# Revit family: Shower-Wall_Supply_Elbow-KOHLER-STATEMENT_WAND-26289W
name_source: partatom
category: Plumbing Fixtures
revit_build: Autodesk Revit 2017 (Build: 20160225_1515(x64)
units: mm (PartAtom-declared; Revit-internal decimal feet)

## family parameters
Cut with Voids When Loaded = No
Host = Face
OmniClass Number = 23.31.17.00
OmniClass Title = Showers
Part Type = Normal
Room Calculation Point = No
Round Connector Dimension = Use Diameter
Shared = No

## types (5) — shared parameters
ADA Compliant = No
Assembly Code = D2010700
CW Connection = No
Cold Water Inlet = Cold Water Inlet
Date Modified = 11/22/2021
Default Elevation = 42"
Description = STATEMENT WAND HS HOLDER W/ SUPPLY
Drain Included = No
Flow Rate = 0 GPM
HW Connection = Yes
Handle Clearance = 2 3/8"
Height = 3 3/4"
Hot Water Inlet = Hot Water Inlet
Length = 2 3/8"
Manufacturer = KOHLER Co.
Master Format 2014 = 22 42 23
Master Format 2014 Name = Residential Showers
Material = Premium Metal Construction
Pressure = 0.00 psi
Product Name = STATEMENT_WAND
Tempered Water Inlet = Tempered Water Inlet
URL = https://www.kohler.co.uk
Vent Connection = No
Waste Connection = No
Waste Water Outlet = Waste Water Outlet
WaterSense Certified = No
Width = 2 1/2"

## per-type parameters (varying)
| type | Finish | Model | Type |
| CP-Polished Chrome | Kohler-Metal-CP-Polished_Chrome | 26289W-CP | 1 |
| BL-Matte Black | Kohler-Metal-BL-Matte_Black | 26289W-BL | 3 |
| BN-Vibrant Brushed Nickel | Kohler-Metal-BN-Vibrant_Brushed_Nickel | 26289W-BN | 2 |
| 2MB-Vibrant Brushed Moderne Brass | Kohler-Metal-2MB-Vibrant_Brushed_Moderne_Brass | 26289W-2MB | 4 |
| BV-Brushed Bronze | Kohler-Metal-BV-Brushed_Bronze | 26289W-BV | 5 |

## geometry (parser evidence)
native form markers: Sweep x6
no freeform markers — native parametric forms only
